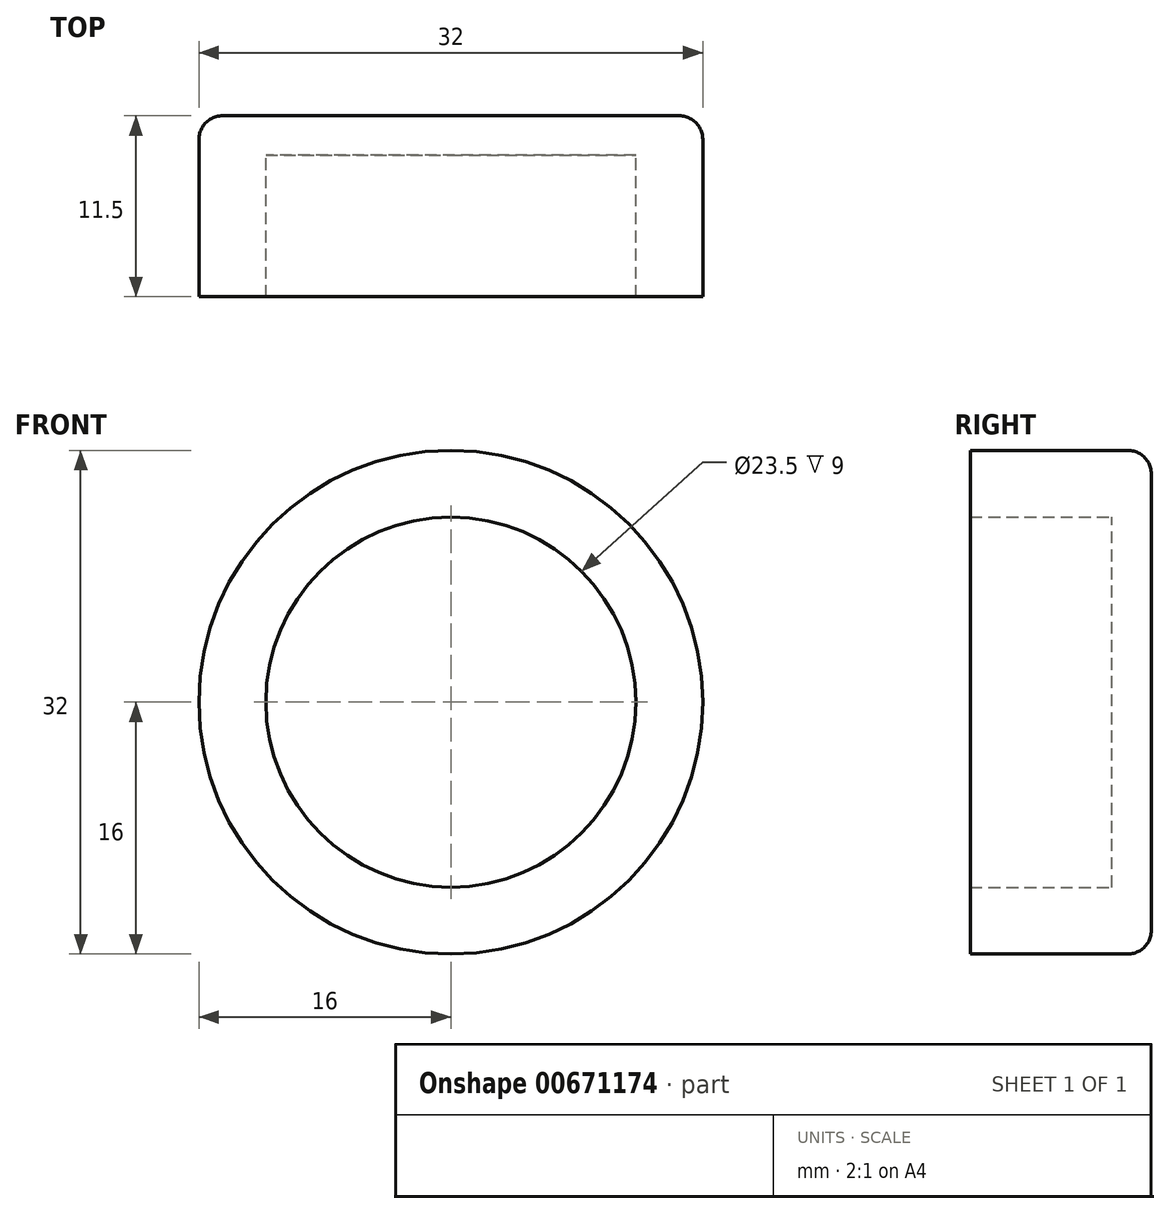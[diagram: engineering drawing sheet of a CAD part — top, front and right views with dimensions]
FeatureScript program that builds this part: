
annotation { "Feature Type Name" : "Feature", "Feature Type Description" : "" }
export const myFeature = defineFeature(function(context is Context, id is Id, definition is map)
    precondition{}
    {
        {
            var Q0;
            Q0=qCreatedBy(makeId("Front.planeOp"),FACE);
            var sketch = newSketch(context, id + "F0", { "sketchPlane" : qUnion([Q0])});
            skCircle(sketch, "E0", {"center": v(0, 0) * mm, "radius": 16 * mm});
            skSolve(sketch);
        }
        {
            var Q0;
            Q0 = qSketchRegion(id + "F0", true);
            extrude(context, id + "F1", {"entities" : qUnion([Q0]), "depth" : 2.5 * mm, "offsetDistance" : 25 * mm});
        }
        {
            var Q0;
            Q0=makeQuery(id+"F1.opExtrude","CAP_FACE",FACE,{"disambiguationData":[OSD([sQuery(id+"F0.wireOp",EDGE,"E0")])],"isStart":false});
            var sketch = newSketch(context, id + "F2", { "sketchPlane" : qUnion([Q0])});
            skCircle(sketch, "E1", {"center": v(0, 0) * mm, "radius": 11.75 * mm});
            skCircle(sketch, "E2", {"center": v(0, 0) * mm, "radius": 16 * mm});
            skSolve(sketch);
        }
        {
            var Q0;
            Q0 = qSketchRegion(id + "F2", true);
            extrude(context, id + "F3", {"entities" : qUnion([Q0]), "operationType" : NewBodyOperationType.ADD, "depth" : 9 * mm, "offsetDistance" : 25 * mm});
        }
        {
            var Q0;
            Q0=makeQuery(id+"F1.opExtrude","CAP_FACE",FACE,{"disambiguationData":[OSD([sQuery(id+"F0.wireOp",EDGE,"E0")])],"isStart":true});
            fillet(context, id + "F4", {"entities" : qUnion([Q0]), "radius" : 1.5 * mm, "tangentPropagation" : true, "allowEdgeOverflow" : false});
        }
    });
